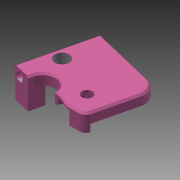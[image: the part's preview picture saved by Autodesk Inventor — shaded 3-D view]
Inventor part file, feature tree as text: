
AUTODESK INVENTOR PART (.ipt)
format: ipt  version: 2014 (Build 180170000, 170)  size: 284,672 bytes
history: native  units: mm
features: other x6, sketch x2, extrude x2
ambient origin geometry x8: Origin, YZ Plane, XZ Plane, XY Plane, X Axis, Y Axis, Z Axis, Center Point
bodies: Solid1 (feature_tree)
feature tree (10):
  other  "spring enhancer.ipt"
  other  "Blocks"
  sketch  "Sketch3"  dims[d0=10.0mm d5=26.0mm]
  extrude  "Extrusion2"  Depth=10.0mm
  extrude  "Extrusion3"  Depth=10.7mm
  other  "Solid1::spring enhancer.ipt"
  other  "TaggingFeature1"
  other  "nema17"
  sketch  "Sketch4"  dims[d7=8.0mm d8=5.8mm d9=10.0mm d10=0.0mm d11=14.3mm d12=5.02mm d13=7.0mm d14=15.0mm d16=10.7mm d17=0.0mm]
  other  "nema17:1"
